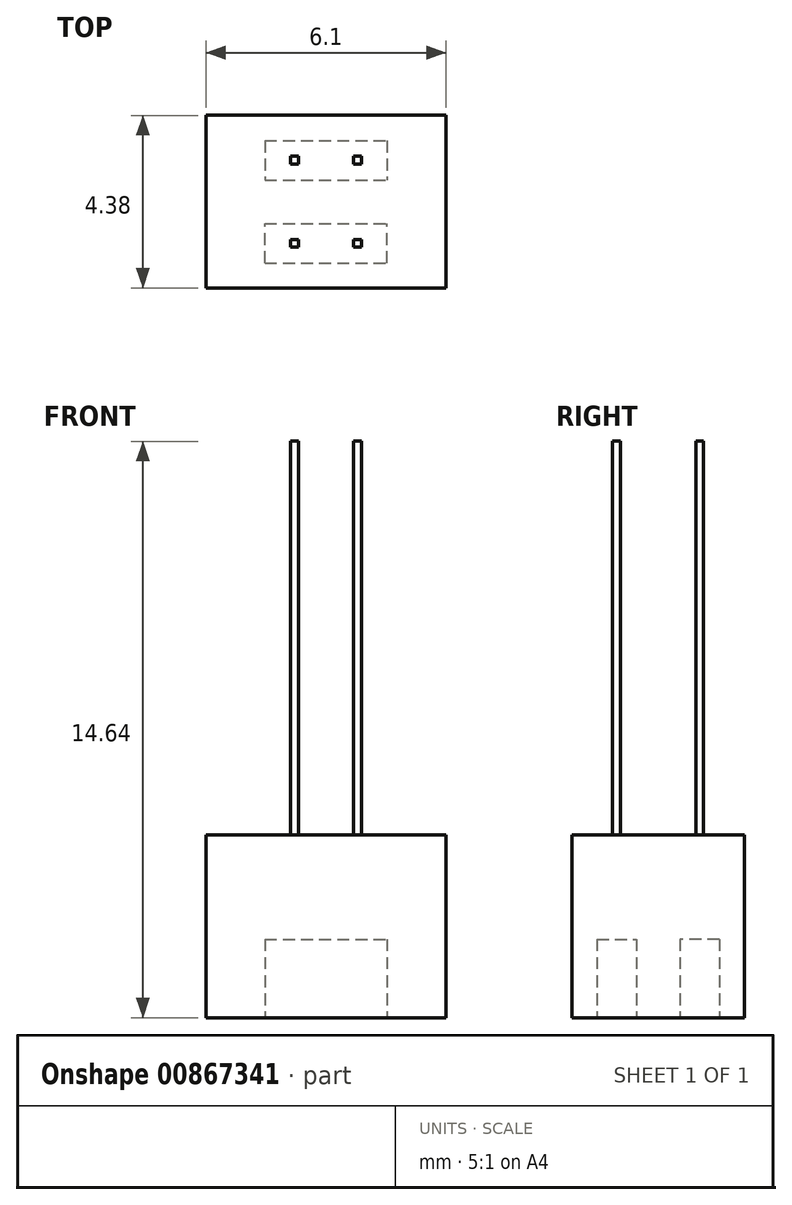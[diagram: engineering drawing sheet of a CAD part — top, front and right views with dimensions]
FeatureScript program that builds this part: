
annotation { "Feature Type Name" : "Feature", "Feature Type Description" : "" }
export const myFeature = defineFeature(function(context is Context, id is Id, definition is map)
    precondition{}
    {
        {
            var Q0;
            Q0=qCreatedBy(makeId("Front.planeOp"),FACE);
            var sketch = newSketch(context, id + "F0", { "sketchPlane" : qUnion([Q0])});
            skLineSegment(sketch, "E0.bottom", {"start": v(3.05, 2.33) * mm, "end": v(-3.05, 2.33) * mm});
            skLineSegment(sketch, "E0.top", {"start": v(3.05, -2.33) * mm, "end": v(-3.05, -2.33) * mm});
            skLineSegment(sketch, "E0.left", {"start": v(3.05, 2.33) * mm, "end": v(3.05, -2.33) * mm});
            skLineSegment(sketch, "E0.right", {"start": v(-3.05, 2.33) * mm, "end": v(-3.05, -2.33) * mm});
            skPoint(sketch, "E0.middle", {"position": v(0, 0) * mm});
            skSolve(sketch);
        }
        {
            var Q0;
            Q0 = qSketchRegion(id + "F0", true);
            extrude(context, id + "F1", {"entities" : qUnion([Q0]), "depth" : 4.39 * mm, "offsetDistance" : 25 * mm, "symmetric" : true});
        }
        {
            var Q0;
            Q0=makeQuery(id+"F1.opExtrude","SWEPT_FACE",FACE,{"disambiguationData":[OSD([sQuery(id+"F0.wireOp",EDGE,"E0.top")])]});
            var sketch = newSketch(context, id + "F2", { "sketchPlane" : qUnion([Q0])});
            skLineSegment(sketch, "E1", {"start": v(0, 1.05) * mm, "end": v(0, -1.05) * mm, "construction": true});
            skLineSegment(sketch, "E2.bottom", {"start": v(-1.55, 1.55) * mm, "end": v(1.55, 1.56) * mm});
            skLineSegment(sketch, "E2.top", {"start": v(-1.55, 0.55) * mm, "end": v(1.55, 0.55) * mm});
            skLineSegment(sketch, "E2.left", {"start": v(-1.55, 1.55) * mm, "end": v(-1.55, 0.55) * mm});
            skLineSegment(sketch, "E2.right", {"start": v(1.55, 1.55) * mm, "end": v(1.55, 0.55) * mm});
            skPoint(sketch, "E2.middle", {"position": v(0, 1.05) * mm});
            skLineSegment(sketch, "E3.bottom", {"start": v(-1.55, -1.55) * mm, "end": v(1.55, -1.55) * mm});
            skLineSegment(sketch, "E3.top", {"start": v(-1.55, -0.55) * mm, "end": v(1.55, -0.55) * mm});
            skLineSegment(sketch, "E3.left", {"start": v(-1.55, -1.55) * mm, "end": v(-1.55, -0.55) * mm});
            skLineSegment(sketch, "E3.right", {"start": v(1.55, -1.55) * mm, "end": v(1.55, -0.55) * mm});
            skPoint(sketch, "E3.middle", {"position": v(0, -1.05) * mm});
            skSolve(sketch);
        }
        {
            var Q0;
            Q0=makeQuery(id+"F1.opExtrude","SWEPT_FACE",FACE,{"disambiguationData":[OSD([sQuery(id+"F0.wireOp",EDGE,"E0.bottom")])]});
            var sketch = newSketch(context, id + "F3", { "sketchPlane" : qUnion([Q0])});
            skLineSegment(sketch, "E4.bottom", {"start": v(0.9, 1.15) * mm, "end": v(0.7, 1.15) * mm});
            skLineSegment(sketch, "E4.top", {"start": v(0.9, 0.96) * mm, "end": v(0.7, 0.95) * mm});
            skLineSegment(sketch, "E4.left", {"start": v(0.9, 1.16) * mm, "end": v(0.9, 0.95) * mm});
            skLineSegment(sketch, "E4.right", {"start": v(0.7, 1.16) * mm, "end": v(0.7, 0.95) * mm});
            skPoint(sketch, "E4.middle", {"position": v(0.8, 1.05) * mm});
            skLineSegment(sketch, "E5", {"start": v(0, 0) * mm, "end": v(0, 1.55) * mm, "construction": true});
            skLineSegment(sketch, "E6", {"start": v(0, 1.05) * mm, "end": v(0.8, 1.05) * mm, "construction": true});
            skPoint(sketch, "E6.startSnap0", {"position": v(0.7, 1.05) * mm});
            skLineSegment(sketch, "E7.MirrorCS", {"start": v(-0.7, 1.16) * mm, "end": v(-0.7, 0.95) * mm});
            skLineSegment(sketch, "E8.MirrorCS", {"start": v(-0.9, 1.16) * mm, "end": v(-0.9, 0.95) * mm});
            skLineSegment(sketch, "E9.MirrorCS", {"start": v(-0.9, 0.96) * mm, "end": v(-0.7, 0.95) * mm});
            skLineSegment(sketch, "E10.MirrorCS", {"start": v(-0.9, 1.15) * mm, "end": v(-0.7, 1.15) * mm});
            skPoint(sketch, "E11.MirrorP", {"position": v(-0.8, 1.05) * mm});
            skPoint(sketch, "E12.MirrorP", {"position": v(-0.7, 1.05) * mm});
            skLineSegment(sketch, "E13", {"start": v(-0.88, 0) * mm, "end": v(0.88, 0) * mm, "construction": true});
            skLineSegment(sketch, "E14.MirrorCS", {"start": v(-0.7, 0.95) * mm, "end": v(-0.7, 1.16) * mm});
            skLineSegment(sketch, "E15.MirrorCS", {"start": v(0.7, 0.95) * mm, "end": v(0.7, 1.16) * mm});
            skLineSegment(sketch, "E16.MirrorCS", {"start": v(-0.9, 0.95) * mm, "end": v(-0.9, 1.16) * mm});
            skLineSegment(sketch, "E17.MirrorCS", {"start": v(-0.9, 0.95) * mm, "end": v(-0.7, 0.96) * mm});
            skLineSegment(sketch, "E18.MirrorCS", {"start": v(0.9, 0.95) * mm, "end": v(0.7, 0.96) * mm});
            skLineSegment(sketch, "E19.MirrorCS", {"start": v(0.9, 0.95) * mm, "end": v(0.9, 1.16) * mm});
            skLineSegment(sketch, "E20.MirrorCS", {"start": v(0.7, -0.95) * mm, "end": v(0.7, -1.16) * mm});
            skLineSegment(sketch, "E21.MirrorCS", {"start": v(0.7, -1.16) * mm, "end": v(0.7, -0.95) * mm});
            skLineSegment(sketch, "E22.MirrorCS", {"start": v(0.9, -1.15) * mm, "end": v(0.7, -1.15) * mm});
            skLineSegment(sketch, "E23.MirrorCS", {"start": v(0.9, -0.95) * mm, "end": v(0.7, -0.96) * mm});
            skPoint(sketch, "E24.MirrorP", {"position": v(0.7, -1.05) * mm});
            skPoint(sketch, "E25.MirrorP", {"position": v(0.8, -1.05) * mm});
            skLineSegment(sketch, "E26.MirrorCS", {"start": v(0.9, -1.16) * mm, "end": v(0.9, -0.95) * mm});
            skLineSegment(sketch, "E27.MirrorCS", {"start": v(0.9, -0.95) * mm, "end": v(0.9, -1.16) * mm});
            skLineSegment(sketch, "E28.MirrorCS", {"start": v(0.9, -0.96) * mm, "end": v(0.7, -0.95) * mm});
            skLineSegment(sketch, "E29.MirrorCS", {"start": v(-0.7, -0.95) * mm, "end": v(-0.7, -1.16) * mm});
            skLineSegment(sketch, "E30.MirrorCS", {"start": v(-0.7, -1.16) * mm, "end": v(-0.7, -0.95) * mm});
            skPoint(sketch, "E31.MirrorP", {"position": v(-0.8, -1.05) * mm});
            skLineSegment(sketch, "E32.MirrorCS", {"start": v(-0.9, -1.16) * mm, "end": v(-0.9, -0.95) * mm});
            skLineSegment(sketch, "E33.MirrorCS", {"start": v(-0.9, -0.96) * mm, "end": v(-0.7, -0.95) * mm});
            skPoint(sketch, "E34.MirrorP", {"position": v(-0.7, -1.05) * mm});
            skLineSegment(sketch, "E35.MirrorCS", {"start": v(-0.9, -1.15) * mm, "end": v(-0.7, -1.15) * mm});
            skLineSegment(sketch, "E36.MirrorCS", {"start": v(-0.9, -0.95) * mm, "end": v(-0.7, -0.96) * mm});
            skLineSegment(sketch, "E37.MirrorCS", {"start": v(-0.9, -0.95) * mm, "end": v(-0.9, -1.16) * mm});
            skSolve(sketch);
        }
        {
            var Q0;
            Q0 = qSketchRegion(id + "F3", true);
            extrude(context, id + "F4", {"entities" : qUnion([Q0]), "operationType" : NewBodyOperationType.ADD, "depth" : 10 * mm, "offsetDistance" : 25 * mm});
        }
        {
            var Q0;
            Q0=makeQuery(id+"F2.imprint","IMPRINT",FACE,{"disambiguationData":[TD([[makeQuery(id+"F2.imprint","IMPRINT",EDGE,{"derivedFrom":sQuery(id+"F2.wireOp",EDGE,"E2.bottom")}),-1.0]])]});
            var Q1;
            Q1=makeQuery(id+"F1.opExtrude","SWEPT_FACE",FACE,{"disambiguationData":[OSD([sQuery(id+"F0.wireOp",EDGE,"E0.top")])]});
            extrude(context, id + "F5", {"entities" : qUnion([Q0]), "oppositeDirection" : true, "depth" : 2 * mm, "endBoundEntityFace" : qUnion([Q1]), "hasOffset" : true, "offsetDistance" : 3 * mm});
        }
        {
            var Q0;
            Q0=makeQuery(id+"F2.imprint","IMPRINT",FACE,{"disambiguationData":[TD([[makeQuery(id+"F2.imprint","IMPRINT",EDGE,{"derivedFrom":sQuery(id+"F2.wireOp",EDGE,"E3.bottom")}),1.0]])]});
            extrude(context, id + "F6", {"entities" : qUnion([Q0]), "oppositeDirection" : true, "depth" : 2 * mm, "offsetDistance" : 25 * mm});
        }
        {
            var Q0;
            Q0=makeQuery(id+"F5.opExtrude","SWEPT_BODY",BODY,{"disambiguationData":[OSD([sQuery(id+"F2.wireOp",EDGE,"E2.bottom"),sQuery(id+"F2.wireOp",EDGE,"E2.top"),sQuery(id+"F2.wireOp",EDGE,"E2.left"),sQuery(id+"F2.wireOp",EDGE,"E2.right")])]});
            var Q1;
            Q1=makeQuery(id+"F6.opExtrude","SWEPT_BODY",BODY,{"disambiguationData":[OSD([sQuery(id+"F2.wireOp",EDGE,"E3.bottom"),sQuery(id+"F2.wireOp",EDGE,"E3.top"),sQuery(id+"F2.wireOp",EDGE,"E3.left"),sQuery(id+"F2.wireOp",EDGE,"E3.right")])]});
            var Q2;
            Q2=makeQuery(id+"F1.opExtrude","SWEPT_BODY",BODY,{"disambiguationData":[OSD([sQuery(id+"F0.wireOp",EDGE,"E0.bottom"),sQuery(id+"F0.wireOp",EDGE,"E0.top"),sQuery(id+"F0.wireOp",EDGE,"E0.left"),sQuery(id+"F0.wireOp",EDGE,"E0.right")])]});
            booleanBodies(context, id + "F7", {"operationType" : BooleanOperationType.SUBTRACTION, "tools" : qUnion([Q0, Q1]), "targets" : qUnion([Q2]), "keepTools" : true});
        }
    });
